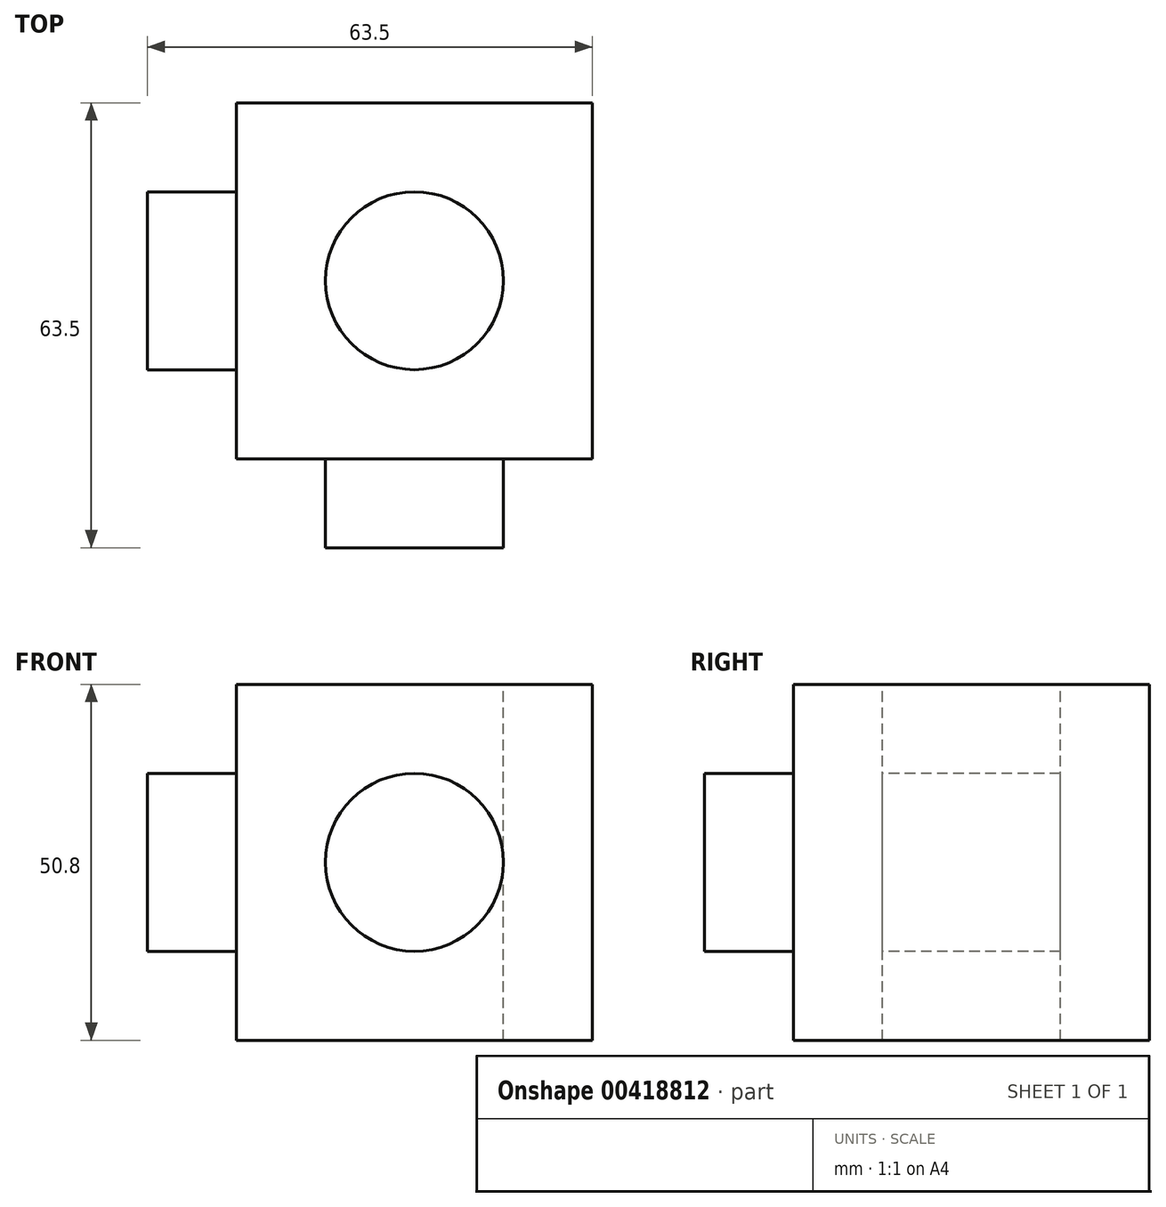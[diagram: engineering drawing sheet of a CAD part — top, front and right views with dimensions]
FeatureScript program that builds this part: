
annotation { "Feature Type Name" : "Feature", "Feature Type Description" : "" }
export const myFeature = defineFeature(function(context is Context, id is Id, definition is map)
    precondition{}
    {
        {
            var Q0;
            Q0=qCreatedBy(makeId("Front.planeOp"),FACE);
            var sketch = newSketch(context, id + "F0", { "sketchPlane" : qUnion([Q0])});
            skLineSegment(sketch, "E0", {"start": v(-50.8, 0) * mm, "end": v(0, 0) * mm});
            skLineSegment(sketch, "E1", {"start": v(0, 0) * mm, "end": v(0, 50.8) * mm});
            skLineSegment(sketch, "E2", {"start": v(0, 50.8) * mm, "end": v(-50.8, 50.8) * mm});
            skLineSegment(sketch, "E3", {"start": v(-50.8, 50.8) * mm, "end": v(-50.8, 0) * mm});
            skSolve(sketch);
        }
        {
            var Q0;
            Q0 = qSketchRegion(id + "F0", true);
            extrude(context, id + "F1", {"entities" : qUnion([Q0]), "depth" : 50.8 * mm});
        }
        {
            var Q0;
            Q0=makeQuery(id+"F1.opExtrude","SWEPT_FACE",FACE,{"disambiguationData":[OSD([sQuery(id+"F0.wireOp",EDGE,"E2")])]});
            var sketch = newSketch(context, id + "F2", { "sketchPlane" : qUnion([Q0])});
            skCircle(sketch, "E4", {"center": v(-25.4, -25.4) * mm, "radius": 12.7 * mm});
            skSolve(sketch);
        }
        {
            var Q0;
            Q0=makeQuery(id+"F2.imprint","IMPRINT",FACE,{"disambiguationData":[TD([[makeQuery(id+"F2.imprint","IMPRINT",EDGE,{"derivedFrom":sQuery(id+"F2.wireOp",EDGE,"E4")}),1.0]])]});
            extrude(context, id + "F3", {"entities" : qUnion([Q0]), "operationType" : NewBodyOperationType.REMOVE, "oppositeDirection" : true, "depth" : 50.8 * mm});
        }
        {
            var Q0;
            Q0=makeQuery(id+"F1.opExtrude","CAP_FACE",FACE,{"disambiguationData":[OSD([sQuery(id+"F0.wireOp",EDGE,"E0"),sQuery(id+"F0.wireOp",EDGE,"E1"),sQuery(id+"F0.wireOp",EDGE,"E2"),sQuery(id+"F0.wireOp",EDGE,"E3")])],"isStart":false});
            var sketch = newSketch(context, id + "F4", { "sketchPlane" : qUnion([Q0])});
            skCircle(sketch, "E5", {"center": v(-25.4, 25.4) * mm, "radius": 12.7 * mm});
            skSolve(sketch);
        }
        {
            var Q0;
            Q0=makeQuery(id+"F4.imprint","IMPRINT",FACE,{"disambiguationData":[TD([[makeQuery(id+"F4.imprint","IMPRINT",EDGE,{"derivedFrom":sQuery(id+"F4.wireOp",EDGE,"E5")}),1.0]])]});
            extrude(context, id + "F5", {"entities" : qUnion([Q0]), "operationType" : NewBodyOperationType.ADD, "depth" : 12.7 * mm});
        }
        {
            var Q0;
            Q0=makeQuery(id+"F1.opExtrude","SWEPT_FACE",FACE,{"disambiguationData":[OSD([sQuery(id+"F0.wireOp",EDGE,"E3")])]});
            var sketch = newSketch(context, id + "F6", { "sketchPlane" : qUnion([Q0])});
            skLineSegment(sketch, "E6.bottom", {"start": v(12.7, 12.7) * mm, "end": v(38.1, 12.7) * mm});
            skLineSegment(sketch, "E6.top", {"start": v(12.7, 38.1) * mm, "end": v(38.1, 38.1) * mm});
            skLineSegment(sketch, "E6.left", {"start": v(12.7, 12.7) * mm, "end": v(12.7, 38.1) * mm});
            skLineSegment(sketch, "E6.right", {"start": v(38.1, 12.7) * mm, "end": v(38.1, 38.1) * mm});
            skSolve(sketch);
        }
        {
            var Q0;
            Q0=makeQuery(id+"F6.imprint","IMPRINT",FACE,{"disambiguationData":[TD([[makeQuery(id+"F6.imprint","IMPRINT",EDGE,{"derivedFrom":sQuery(id+"F6.wireOp",EDGE,"E6.bottom")}),1.0]])]});
            extrude(context, id + "F7", {"entities" : qUnion([Q0]), "operationType" : NewBodyOperationType.ADD, "depth" : 12.7 * mm});
        }
    });
